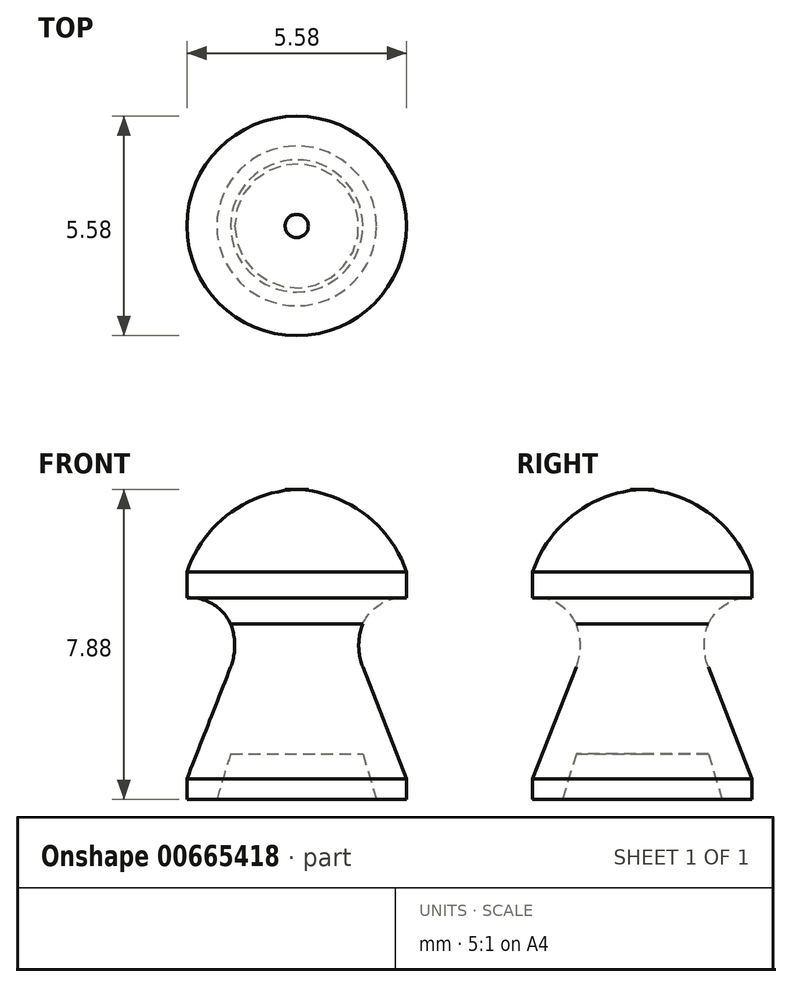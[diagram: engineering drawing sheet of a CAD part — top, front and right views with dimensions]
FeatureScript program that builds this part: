
annotation { "Feature Type Name" : "Feature", "Feature Type Description" : "" }
export const myFeature = defineFeature(function(context is Context, id is Id, definition is map)
    precondition{}
    {
        {
            var Q0;
            Q0=qCreatedBy(makeId("Front.planeOp"),FACE);
            var sketch = newSketch(context, id + "F0", { "sketchPlane" : qUnion([Q0])});
            skLineSegment(sketch, "E0", {"start": v(2.03, 0) * mm, "end": v(2.79, 0) * mm});
            skLineSegment(sketch, "E1", {"start": v(2.79, 0) * mm, "end": v(2.79, 0.52) * mm});
            skLineSegment(sketch, "E2", {"start": v(2.79, 0.52) * mm, "end": v(1.68, 3.36) * mm});
            skArc(sketch, "E3", {"start": v(1.68, 4.46) * mm, "mid": v(1.57, 3.9) * mm, "end": v(1.68, 3.36) * mm});
            skArc(sketch, "E4", {"start": v(2.79, 5.12) * mm, "mid": v(2.13, 4.96) * mm, "end": v(1.68, 4.46) * mm});
            skLineSegment(sketch, "E5", {"start": v(0, 1.16) * mm, "end": v(0, 7.55) * mm});
            skLineSegment(sketch, "E6", {"start": v(2.03, 0) * mm, "end": v(1.68, 1.16) * mm});
            skLineSegment(sketch, "E7", {"start": v(1.68, 1.16) * mm, "end": v(0, 1.16) * mm});
            skLineSegment(sketch, "E8", {"start": v(2.79, 5.12) * mm, "end": v(2.79, 5.78) * mm});
            skArc(sketch, "E9", {"start": v(2.79, 5.78) * mm, "mid": v(1.72, 7.26) * mm, "end": v(0, 7.88) * mm});
            skLineSegment(sketch, "E10", {"start": v(0, 7.55) * mm, "end": v(0, 7.88) * mm});
            skSolve(sketch);
        }
        {
            var Q0;
            Q0=makeQuery(id+"F0.imprint","IMPRINT",FACE,{"disambiguationData":[TD([[makeQuery(id+"F0.imprint","IMPRINT",EDGE,{"derivedFrom":sQuery(id+"F0.wireOp",EDGE,"E0")}),1.0]])]});
            var Q1;
            Q1=sQuery(id+"F0.wireOp",EDGE,"E5");
            revolve(context, id + "F1", {"surfaceOperationType" : NewSurfaceOperationType.NEW, "entities" : qUnion([Q0]), "axis" : qUnion([Q1]), "revolveType" : RevolveType.FULL});
        }
    });
